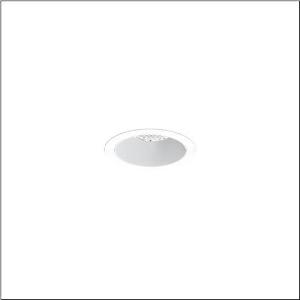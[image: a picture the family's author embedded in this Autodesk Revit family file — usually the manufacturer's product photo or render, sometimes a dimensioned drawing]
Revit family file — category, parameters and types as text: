
# Revit family: lunis_21_m_51db18mc91c
name_source: partatom
category: Lighting Fixtures
units: mm (PartAtom-declared; Revit-internal decimal feet)

## family parameters
Cut with Voids When Loaded = No
Host = Face
Light Source = No
Part Type = Normal
Room Calculation Point = No
Round Connector Dimension = Use Diameter
Shared = No

## types (1)
- --- (1 x LED, 4040 lm, 25.5 W, 4000K)
    Apparent Load = 26 VA
    CIE Flux Codes = 95 100 100 100 100
    Color Rendering = 80
    Color Temperature = 4000K
    Default Elevation = 1800 mm
    Description = Lunis 21,  M, downlight, light control with lens, of PMMA, anti glare with reflector, of PC, light emission: direct distribution, LED rated luminous flux: 1.840lm, light colour: 830/840/865, with terminal, 3-pole, mains connection: 220..240V, AC/DC, 0/50..60Hz, housing, round, of diecast aluminium, traffic white (RAL 9016), diameter: 115mm, clamping range: 1..40mm, protection rating (complete): IP20, protection rating (on room side): IP54, insulation class (complete): insulation class II (safety insulation), certification: CE, impact resistance: IK03, packaging unit: 1 piece
    Height = 0 mm  [stored 0 ft]
    Lamp = 1 x LED
    Lamp Light Flux = 4040 lm
    Lamp Power = 25.5 W
    Lamp count = 1
    Length = 115 mm
    Luminous efficacy = 158 lm/W
    Manufacturer = Siteco
    ModVariant = No
    Model = 51DB18MC91C
    Mounting Place = Ceiling
    Mounting Type = Recessed
    Number of Poles = 1
    OnlyDefault = Yes
    Power Factor = 1
    Product Name = Lunis 21 M
    Product group = downlight
    ProductGroupID = 400
    Protection Class = Protection class II
    Protection Degree = IP 20
    RLX_Detail_Level = 1
    RLX_Emergency_Light_Flux = 0 lm
    RLX_Emergency_Type = 0
    RLX_Emergency_Type_DB = No
    RlxData = <blob elided: 10593 chars, md5=358cb8a2>
    Socket = socket
    Standby Power = 0 W
    System Light Flux = 4040 lm
    System Power = 26 W
    Type Comments = individual setting: colour temperature 4000K, luminous flux: 100 % | (ON | ON | OFF | OFF) | 700 mA
    Type Image = l_1290852.jpg
    URL = http://relux.com
    VarID = @adj_017775
    Voltage = 0 V
    Weight = 0.00 kg
    Width = 0 mm  [stored 0 ft]

note: [stored X ft] marks values corroborated as IEEE doubles in the binary element streams (Revit-internal decimal feet)

## geometry (parser evidence)
native form markers: Sweep x7
no freeform markers — native parametric forms only
